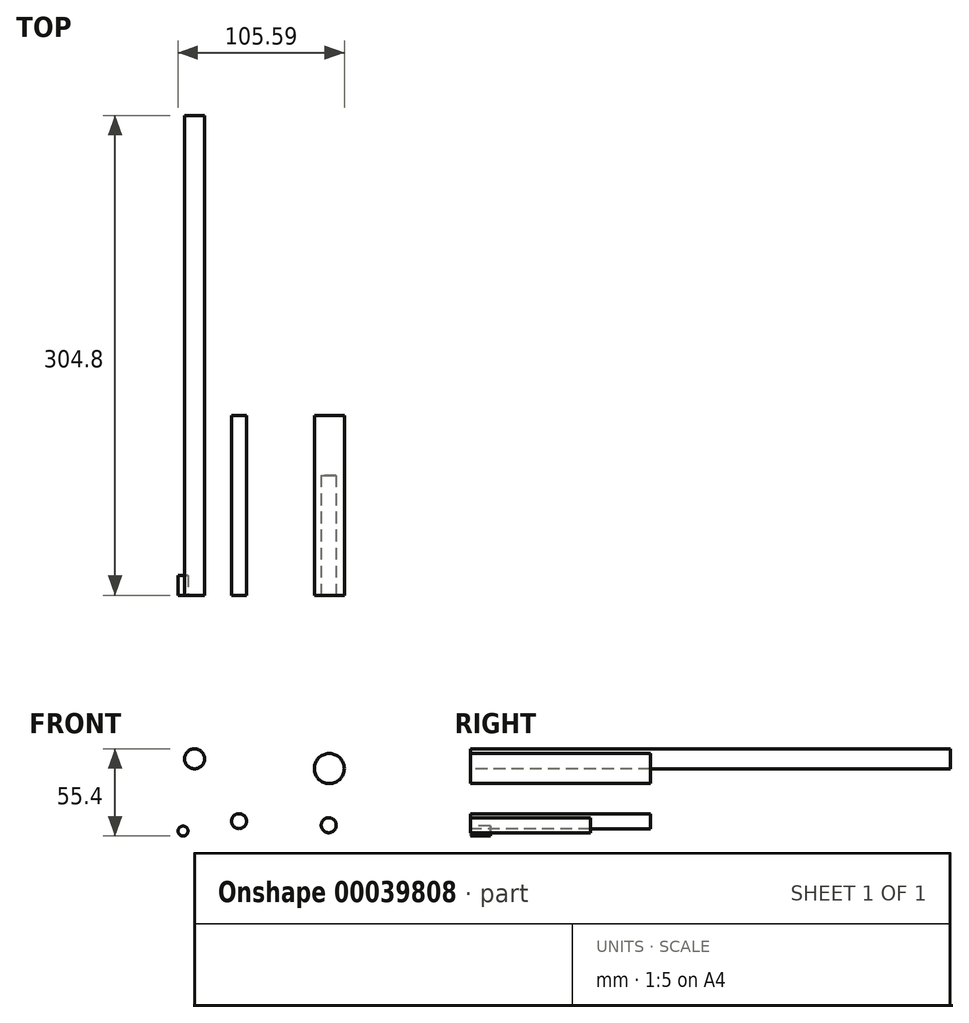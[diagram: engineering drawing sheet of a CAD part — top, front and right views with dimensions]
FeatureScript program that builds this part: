
annotation { "Feature Type Name" : "Feature", "Feature Type Description" : "" }
export const myFeature = defineFeature(function(context is Context, id is Id, definition is map)
    precondition{}
    {
        {
            var Q0;
            Q0=qCreatedBy(makeId("Front.planeOp"),FACE);
            var sketch = newSketch(context, id + "F0", { "sketchPlane" : qUnion([Q0])});
            skCircle(sketch, "E0", {"center": v(-47.8, 39.6) * mm, "radius": 6.35 * mm});
            skSolve(sketch);
        }
        {
            var Q0;
            Q0=makeQuery(id+"F0.imprint","IMPRINT",FACE,{"disambiguationData":[TD([[makeQuery(id+"F0.imprint","IMPRINT",EDGE,{"derivedFrom":sQuery(id+"F0.wireOp",EDGE,"E0")}),1.0]])]});
            extrude(context, id + "F1", {"entities" : qUnion([Q0]), "oppositeDirection" : true, "depth" : 304.8 * mm});
        }
        {
            var Q0;
            Q0=qCreatedBy(makeId("Front.planeOp"),FACE);
            var sketch = newSketch(context, id + "F2", { "sketchPlane" : qUnion([Q0])});
            skCircle(sketch, "E1", {"center": v(37.8, 33.4) * mm, "radius": 9.53 * mm});
            skSolve(sketch);
        }
        {
            var Q0;
            Q0=makeQuery(id+"F2.imprint","IMPRINT",FACE,{"disambiguationData":[TD([[makeQuery(id+"F2.imprint","IMPRINT",EDGE,{"derivedFrom":sQuery(id+"F2.wireOp",EDGE,"E1")}),1.0]])]});
            extrude(context, id + "F3", {"entities" : qUnion([Q0]), "oppositeDirection" : true, "depth" : 114.3 * mm});
        }
        {
            var Q0;
            Q0=qCreatedBy(makeId("Front.planeOp"),FACE);
            var sketch = newSketch(context, id + "F4", { "sketchPlane" : qUnion([Q0])});
            skCircle(sketch, "E2", {"center": v(-19.54, 0) * mm, "radius": 4.76 * mm});
            skSolve(sketch);
        }
        {
            var Q0;
            Q0=makeQuery(id+"F4.imprint","IMPRINT",FACE,{"disambiguationData":[TD([[makeQuery(id+"F4.imprint","IMPRINT",EDGE,{"derivedFrom":sQuery(id+"F4.wireOp",EDGE,"E2")}),1.0]])]});
            extrude(context, id + "F5", {"entities" : qUnion([Q0]), "oppositeDirection" : true, "depth" : 114.3 * mm});
        }
        {
            var Q0;
            Q0=qCreatedBy(makeId("Front.planeOp"),FACE);
            var sketch = newSketch(context, id + "F6", { "sketchPlane" : qUnion([Q0])});
            skCircle(sketch, "E3", {"center": v(37.42, -2.62) * mm, "radius": 4.76 * mm});
            skSolve(sketch);
        }
        {
            var Q0;
            Q0=makeQuery(id+"F6.imprint","IMPRINT",FACE,{"disambiguationData":[TD([[makeQuery(id+"F6.imprint","IMPRINT",EDGE,{"derivedFrom":sQuery(id+"F6.wireOp",EDGE,"E3")}),1.0]])]});
            extrude(context, id + "F7", {"entities" : qUnion([Q0]), "oppositeDirection" : true, "depth" : 76.2 * mm});
        }
        {
            var Q0;
            Q0=qCreatedBy(makeId("Front.planeOp"),FACE);
            var sketch = newSketch(context, id + "F8", { "sketchPlane" : qUnion([Q0])});
            skCircle(sketch, "E4", {"center": v(-55.1, -6.28) * mm, "radius": 3.18 * mm});
            skSolve(sketch);
        }
        {
            var Q0;
            Q0=makeQuery(id+"F8.imprint","IMPRINT",FACE,{"disambiguationData":[TD([[makeQuery(id+"F8.imprint","IMPRINT",EDGE,{"derivedFrom":sQuery(id+"F8.wireOp",EDGE,"E4")}),1.0]])]});
            extrude(context, id + "F9", {"entities" : qUnion([Q0]), "oppositeDirection" : true, "depth" : 12.7 * mm});
        }
    });
